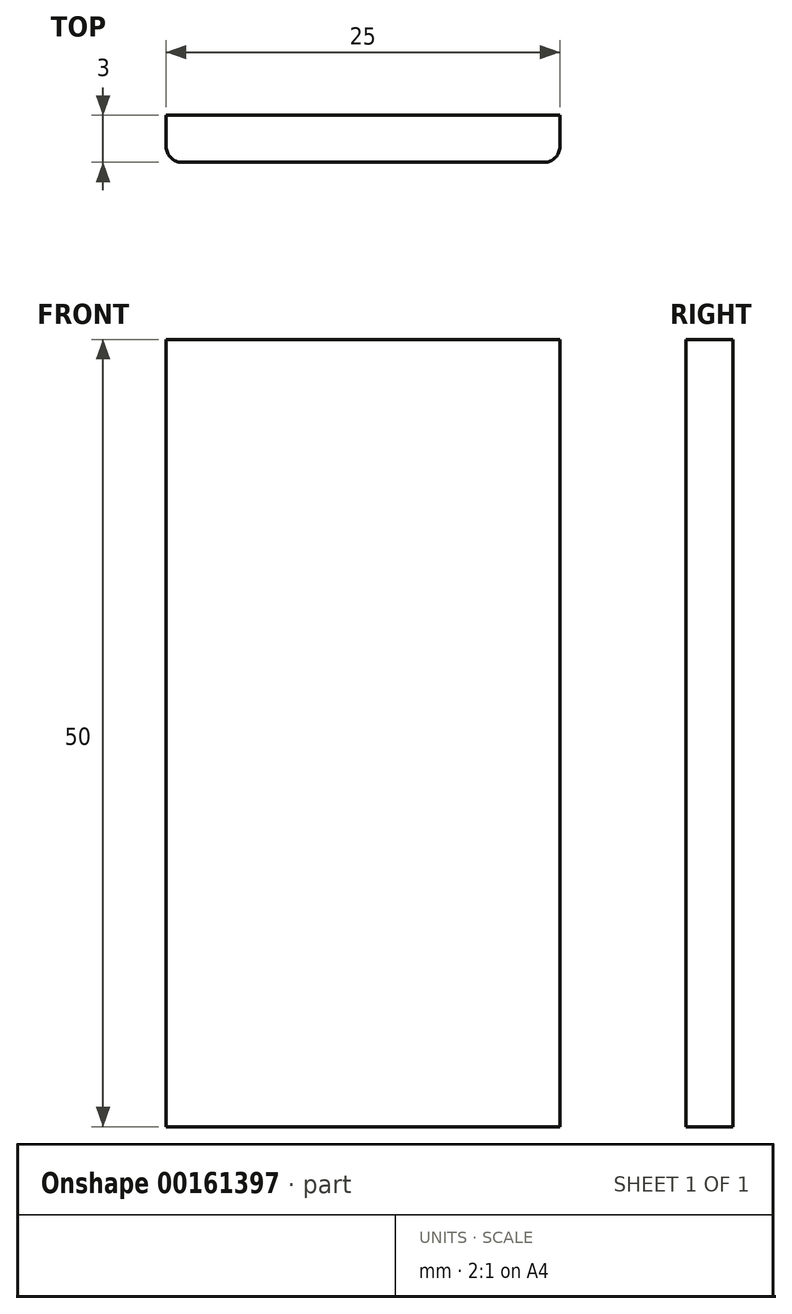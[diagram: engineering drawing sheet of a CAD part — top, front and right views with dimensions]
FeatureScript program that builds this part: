
annotation { "Feature Type Name" : "Feature", "Feature Type Description" : "" }
export const myFeature = defineFeature(function(context is Context, id is Id, definition is map)
    precondition{}
    {
        {
            var Q0;
            Q0=qCreatedBy(makeId("Front.planeOp"),FACE);
            var sketch = newSketch(context, id + "F0", { "sketchPlane" : qUnion([Q0])});
            skLineSegment(sketch, "E0.bottom", {"start": v(-23.7, 15.58) * mm, "end": v(1.3, 15.58) * mm});
            skLineSegment(sketch, "E0.top", {"start": v(-23.7, -34.42) * mm, "end": v(1.3, -34.42) * mm});
            skLineSegment(sketch, "E0.left", {"start": v(-23.7, 15.58) * mm, "end": v(-23.7, -34.42) * mm});
            skLineSegment(sketch, "E0.right", {"start": v(1.3, 15.58) * mm, "end": v(1.3, -34.42) * mm});
            skSolve(sketch);
        }
        {
            var Q0;
            Q0 = qSketchRegion(id + "F0", true);
            extrude(context, id + "F1", {"entities" : qUnion([Q0]), "depth" : 3 * mm});
        }
        {
            var Q0;
            Q0=makeQuery(id+"F1.opExtrude","CAP_EDGE",EDGE,{"disambiguationData":[OSD([sQuery(id+"F0.wireOp",EDGE,"E0.left")])],"isStart":false});
            var Q1;
            Q1=makeQuery(id+"F1.opExtrude","CAP_EDGE",EDGE,{"disambiguationData":[OSD([sQuery(id+"F0.wireOp",EDGE,"E0.right")])],"isStart":false});
            var Q2;
            Q2=makeQuery(id+"FRFbIoxZIdXuPJl_1.opExtrude","CAP_EDGE",EDGE,{"disambiguationData":[OSD([sQuery(id+"FXepa2PaUFyBDLQ_1.wireOp",EDGE,"A6H6ucS5-YKy4-ceby-ZeCu-K94599UxRYdR.left")])],"isStart":false});
            var Q3;
            Q3=makeQuery(id+"FRFbIoxZIdXuPJl_1.opExtrude","CAP_EDGE",EDGE,{"disambiguationData":[OSD([sQuery(id+"FXepa2PaUFyBDLQ_1.wireOp",EDGE,"A6H6ucS5-YKy4-ceby-ZeCu-K94599UxRYdR.right")])],"isStart":false});
            fillet(context, id + "F2", {"entities" : qUnion([Q0, Q1, Q2, Q3]), "radius" : 1 * mm, "tangentPropagation" : true, "allowEdgeOverflow" : false});
        }
    });
